# Revit family: 84546_HOST_FACE
name_source: partatom
category: Lighting Fixtures
revit_build: Autodesk Revit MEP 2015 (Build: 20140606_1530(x64)
units: mm (PartAtom-declared; Revit-internal decimal feet)

## types (4) — shared parameters
Color Filter = 16777215
Dimming Lamp Color Temperature Shift = <None>
Manufacturer = BEGA-US
Telephone = 805.684.0533
URL = www.bega-us.com

## per-type parameters (varying)
| type | Default Elevation | Description | Lamp | Model | Photometric Web File | Tilt Angle |
| Wall Luminaires - Directed Light | 6' - 0" | Surface wall with cutoff optics | 44.6W LED | 2260LED | generic | 90.00° |
| Wall Luminaires - Linear | 6' - 0" | Suface wall - linear with white acrylic diffuser | (1) 39W CF twin-4-p | 4425P | generic | 90.00° |
| Ceiling and Wall Luminaires - Unshielded | 6' - 0" | LED ceiling and wall luminaires - impact resistant | 8.4W LED | 33 508 | 33508.ies | 90.00° |
| Floodlights - Small Scale | 0' - 0" | Performance floodlight - wide beam | 71.1W LED | 84545 | 84546K3.ies | 0.00° |

## geometry (parser evidence)
native form markers: Blend x7, Sweep x12
no freeform markers — native parametric forms only
